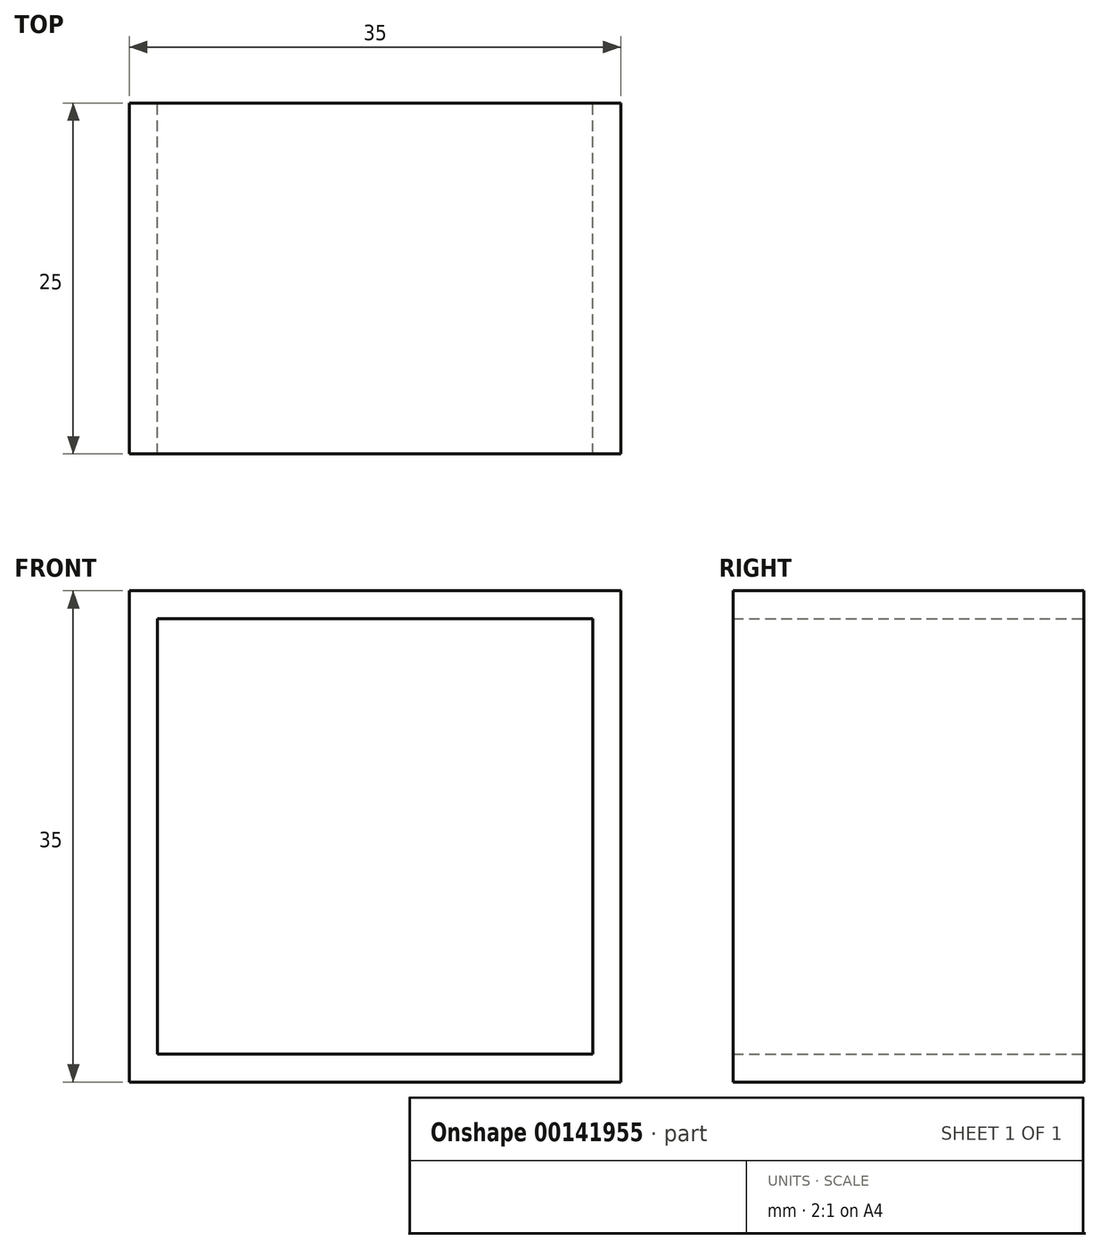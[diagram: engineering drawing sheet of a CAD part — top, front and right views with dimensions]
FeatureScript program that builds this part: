
annotation { "Feature Type Name" : "Feature", "Feature Type Description" : "" }
export const myFeature = defineFeature(function(context is Context, id is Id, definition is map)
    precondition{}
    {
        {
            var Q0;
            Q0=qCreatedBy(makeId("Front.planeOp"),FACE);
            var sketch = newSketch(context, id + "F0", { "sketchPlane" : qUnion([Q0])});
            skLineSegment(sketch, "E0.bottom", {"start": v(-18.8, 7.15) * mm, "end": v(12.2, 7.15) * mm});
            skLineSegment(sketch, "E0.top", {"start": v(-18.8, -23.85) * mm, "end": v(12.2, -23.85) * mm});
            skLineSegment(sketch, "E0.left", {"start": v(-18.8, 7.15) * mm, "end": v(-18.8, -23.85) * mm});
            skLineSegment(sketch, "E0.right", {"start": v(12.2, 7.15) * mm, "end": v(12.2, -23.85) * mm});
            skLineSegment(sketch, "E1.bottom", {"start": v(-20.8, 9.15) * mm, "end": v(14.2, 9.15) * mm});
            skLineSegment(sketch, "E1.top", {"start": v(-20.8, -25.85) * mm, "end": v(14.2, -25.85) * mm});
            skLineSegment(sketch, "E1.left", {"start": v(-20.8, 9.15) * mm, "end": v(-20.8, -25.85) * mm});
            skLineSegment(sketch, "E1.right", {"start": v(14.2, 9.15) * mm, "end": v(14.2, -25.85) * mm});
            skSolve(sketch);
        }
        {
            var Q0;
            Q0=makeQuery(id+"F0.imprint","IMPRINT",FACE,{"disambiguationData":[TD([[makeQuery(id+"F0.imprint","IMPRINT",EDGE,{"derivedFrom":sQuery(id+"F0.wireOp",EDGE,"E0.bottom")}),1.0]])]});
            extrude(context, id + "F1", {"entities" : qUnion([Q0]), "depth" : 25 * mm, "offsetDistance" : 25 * mm});
        }
    });
